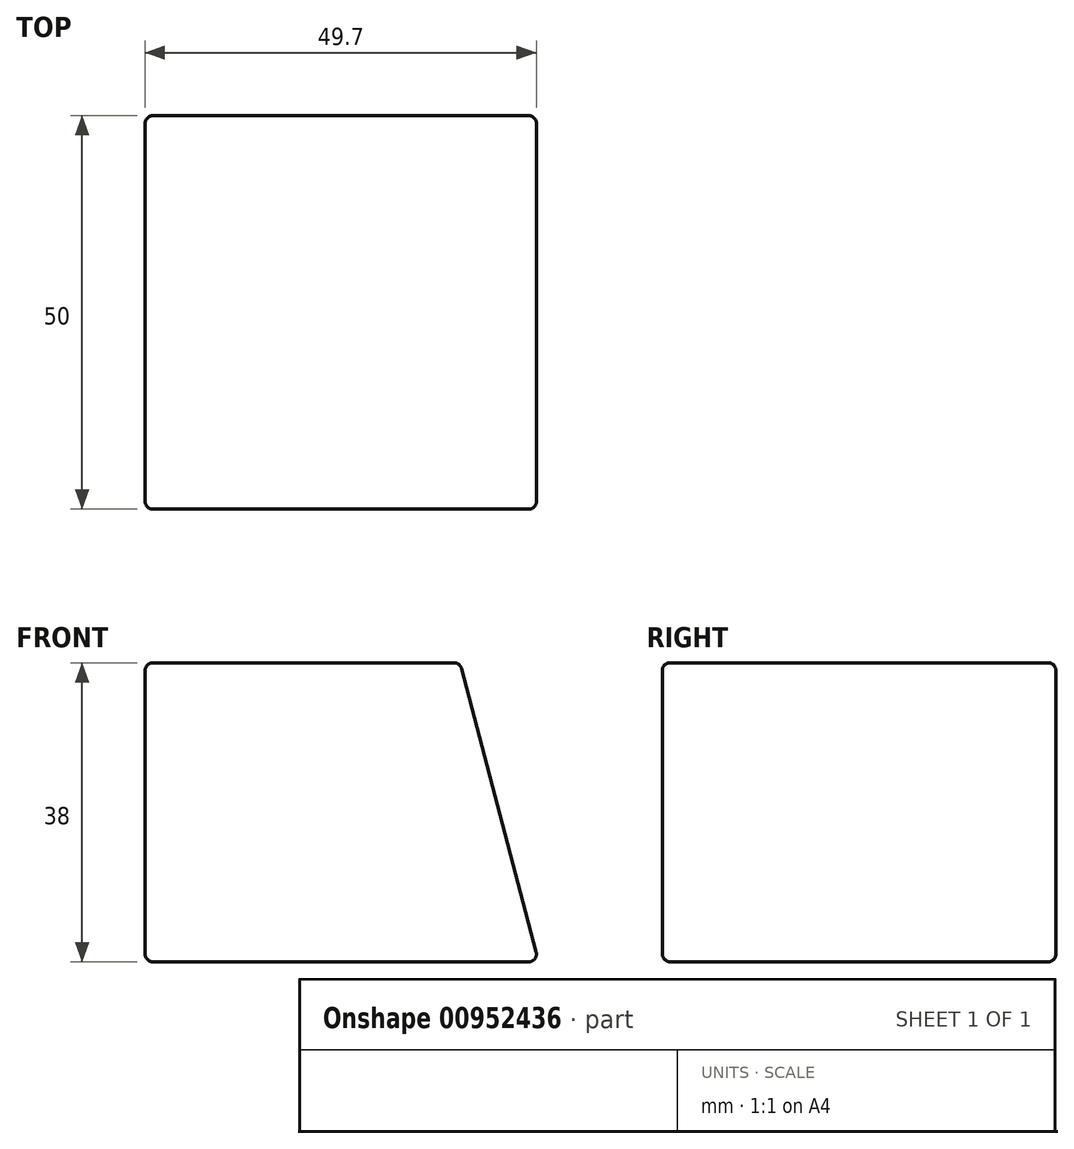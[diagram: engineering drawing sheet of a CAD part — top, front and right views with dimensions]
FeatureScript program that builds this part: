
annotation { "Feature Type Name" : "Feature", "Feature Type Description" : "" }
export const myFeature = defineFeature(function(context is Context, id is Id, definition is map)
    precondition{}
    {
        {
            var Q0;
            Q0=qCreatedBy(makeId("Front.planeOp"),FACE);
            var sketch = newSketch(context, id + "F0", { "sketchPlane" : qUnion([Q0])});
            skLineSegment(sketch, "E0", {"start": v(0, 0) * mm, "end": v(50, 0) * mm});
            skLineSegment(sketch, "E1", {"start": v(50, 0) * mm, "end": v(40, 38) * mm});
            skLineSegment(sketch, "E2", {"start": v(40, 38) * mm, "end": v(0, 38) * mm});
            skLineSegment(sketch, "E3", {"start": v(0, 38) * mm, "end": v(0, 0) * mm});
            skSolve(sketch);
        }
        {
            var Q0;
            Q0=makeQuery(id+"F0.imprint","IMPRINT",FACE,{"disambiguationData":[TD([[makeQuery(id+"F0.imprint","IMPRINT",EDGE,{"derivedFrom":sQuery(id+"F0.wireOp",EDGE,"E0")}),1.0]])]});
            extrude(context, id + "F1", {"entities" : qUnion([Q0]), "depth" : 50 * mm, "offsetDistance" : 25 * mm});
        }
        {
            var Q0;
            Q0=makeQuery(id+"F1.opExtrude","SWEPT_FACE",FACE,{"disambiguationData":[OSD([sQuery(id+"F0.wireOp",EDGE,"E2")])]});
            var Q1;
            Q1=makeQuery(id+"F1.opExtrude","SWEPT_FACE",FACE,{"disambiguationData":[OSD([sQuery(id+"F0.wireOp",EDGE,"E0")])]});
            var Q2;
            Q2=makeQuery(id+"F1.opExtrude","CAP_FACE",FACE,{"disambiguationData":[OSD([sQuery(id+"F0.wireOp",EDGE,"E0"),sQuery(id+"F0.wireOp",EDGE,"E1"),sQuery(id+"F0.wireOp",EDGE,"E2"),sQuery(id+"F0.wireOp",EDGE,"E3")])],"isStart":false});
            var Q3;
            Q3=makeQuery(id+"F1.opExtrude","SWEPT_FACE",FACE,{"disambiguationData":[OSD([sQuery(id+"F0.wireOp",EDGE,"E1")])]});
            var Q4;
            Q4=makeQuery(id+"F1.opExtrude","CAP_FACE",FACE,{"disambiguationData":[OSD([sQuery(id+"F0.wireOp",EDGE,"E0"),sQuery(id+"F0.wireOp",EDGE,"E1"),sQuery(id+"F0.wireOp",EDGE,"E2"),sQuery(id+"F0.wireOp",EDGE,"E3")])],"isStart":true});
            var Q5;
            Q5=makeQuery(id+"F1.opExtrude","SWEPT_FACE",FACE,{"disambiguationData":[OSD([sQuery(id+"F0.wireOp",EDGE,"E3")])]});
            fillet(context, id + "F2", {"entities" : qUnion([Q0, Q1, Q2, Q3, Q4, Q5]), "radius" : 1 * mm, "tangentPropagation" : true, "allowEdgeOverflow" : false});
        }
    });
